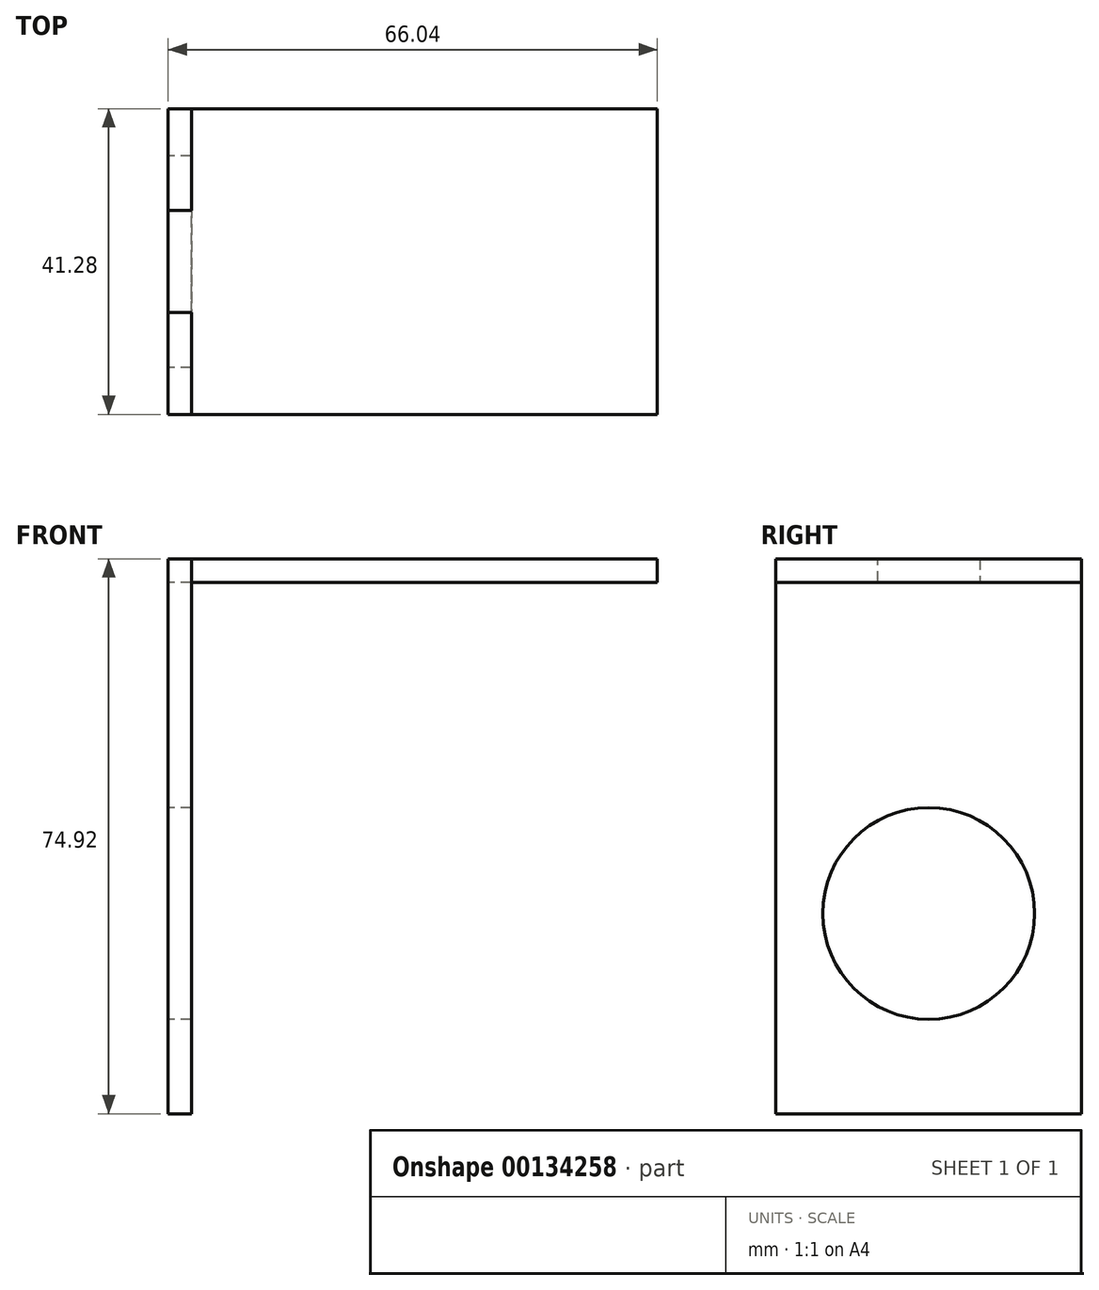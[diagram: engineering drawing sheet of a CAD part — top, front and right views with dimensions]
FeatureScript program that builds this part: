
annotation { "Feature Type Name" : "Feature", "Feature Type Description" : "" }
export const myFeature = defineFeature(function(context is Context, id is Id, definition is map)
    precondition{}
    {
        {
            var Q0;
            Q0=qCreatedBy(makeId("Top.planeOp"),FACE);
            var sketch = newSketch(context, id + "F0", { "sketchPlane" : qUnion([Q0])});
            skLineSegment(sketch, "E0.bottom", {"start": v(-33.02, 20.64) * mm, "end": v(33.02, 20.64) * mm});
            skLineSegment(sketch, "E0.top", {"start": v(-33.02, -20.64) * mm, "end": v(33.02, -20.64) * mm});
            skLineSegment(sketch, "E0.left", {"start": v(-33.02, 20.64) * mm, "end": v(-33.02, -20.64) * mm});
            skLineSegment(sketch, "E0.right", {"start": v(33.02, 20.64) * mm, "end": v(33.02, -20.64) * mm});
            skPoint(sketch, "E0.middle", {"position": v(0, 0) * mm});
            skSolve(sketch);
        }
        {
            var Q0;
            Q0=qSketchRegion(id+"F0",true);
            extrude(context, id + "F1", {"entities" : qUnion([Q0]), "depth" : 3.17 * mm});
        }
        {
            var Q0;
            Q0=makeQuery(id+"F1.opExtrude","CAP_FACE",FACE,{"disambiguationData":[OSD([sQuery(id+"F0.wireOp",EDGE,"E0.bottom"),sQuery(id+"F0.wireOp",EDGE,"E0.top"),sQuery(id+"F0.wireOp",EDGE,"E0.left"),sQuery(id+"F0.wireOp",EDGE,"E0.right")])],"isStart":true});
            var sketch = newSketch(context, id + "F2", { "sketchPlane" : qUnion([Q0])});
            skLineSegment(sketch, "E1.bottom", {"start": v(-33.02, 20.64) * mm, "end": v(-29.85, 20.64) * mm});
            skLineSegment(sketch, "E1.top", {"start": v(-33.02, -20.64) * mm, "end": v(-29.85, -20.64) * mm});
            skLineSegment(sketch, "E1.left", {"start": v(-33.02, 20.64) * mm, "end": v(-33.02, -20.64) * mm});
            skLineSegment(sketch, "E1.right", {"start": v(-29.85, 20.64) * mm, "end": v(-29.85, -20.64) * mm});
            skSolve(sketch);
        }
        {
            var Q0;
            Q0=qSketchRegion(id+"F2",true);
            extrude(context, id + "F3", {"entities" : qUnion([Q0]), "depth" : 71.75 * mm});
        }
        {
            var Q0;
            Q0=makeQuery(id+"F1.opExtrude","SWEPT_FACE",FACE,{"disambiguationData":[OSD([sQuery(id+"F0.wireOp",EDGE,"E0.left")])]});
            var sketch = newSketch(context, id + "F4", { "sketchPlane" : qUnion([Q0])});
            skLineSegment(sketch, "E2.bottom", {"start": v(-20.64, 3.18) * mm, "end": v(-6.88, 3.18) * mm});
            skLineSegment(sketch, "E2.top", {"start": v(-20.64, 0) * mm, "end": v(-6.88, 0) * mm});
            skLineSegment(sketch, "E2.left", {"start": v(-20.64, 3.18) * mm, "end": v(-20.64, 0) * mm});
            skLineSegment(sketch, "E2.right", {"start": v(-6.88, 3.18) * mm, "end": v(-6.88, 0) * mm});
            skLineSegment(sketch, "E3.bottom", {"start": v(-6.88, 0) * mm, "end": v(6.88, 0) * mm});
            skLineSegment(sketch, "E3.top", {"start": v(-6.88, 3.18) * mm, "end": v(6.88, 3.18) * mm});
            skLineSegment(sketch, "E3.left", {"start": v(-6.88, 0) * mm, "end": v(-6.88, 3.18) * mm});
            skLineSegment(sketch, "E3.right", {"start": v(6.88, 0) * mm, "end": v(6.88, 3.18) * mm});
            skLineSegment(sketch, "E4.bottom", {"start": v(6.88, 3.18) * mm, "end": v(20.64, 3.18) * mm});
            skLineSegment(sketch, "E4.top", {"start": v(6.88, 0) * mm, "end": v(20.64, 0) * mm});
            skLineSegment(sketch, "E4.left", {"start": v(6.88, 3.18) * mm, "end": v(6.88, 0) * mm});
            skLineSegment(sketch, "E4.right", {"start": v(20.64, 3.18) * mm, "end": v(20.64, 0) * mm});
            skSolve(sketch);
        }
        {
            var Q0;
            Q0=makeQuery(id+"F4.imprint","IMPRINT",FACE,{"disambiguationData":[TD([[makeQuery(id+"F4.imprint","IMPRINT",EDGE,{"derivedFrom":sQuery(id+"F4.wireOp",EDGE,"E2.bottom")}),-1.0]])]});
            var Q1;
            Q1=makeQuery(id+"F4.imprint","IMPRINT",FACE,{"disambiguationData":[TD([[makeQuery(id+"F4.imprint","IMPRINT",EDGE,{"derivedFrom":sQuery(id+"F4.wireOp",EDGE,"E4.bottom")}),-1.0]])]});
            extrude(context, id + "F5", {"entities" : qUnion([Q0, Q1]), "oppositeDirection" : true, "depth" : 3.17 * mm});
        }
        {
            var Q0;
            Q0=makeQuery(id+"F5.opExtrude","SWEPT_BODY",BODY,{"disambiguationData":[OSD([sQuery(id+"F4.wireOp",EDGE,"E4.bottom"),sQuery(id+"F4.wireOp",EDGE,"E4.top"),sQuery(id+"F4.wireOp",EDGE,"E4.left"),sQuery(id+"F4.wireOp",EDGE,"E4.right")])]});
            var Q1;
            Q1=makeQuery(id+"F5.opExtrude","SWEPT_BODY",BODY,{"disambiguationData":[OSD([sQuery(id+"F4.wireOp",EDGE,"E2.bottom"),sQuery(id+"F4.wireOp",EDGE,"E2.top"),sQuery(id+"F4.wireOp",EDGE,"E2.left"),sQuery(id+"F4.wireOp",EDGE,"E3.left")])]});
            var Q2;
            Q2=makeQuery(id+"F1.opExtrude","SWEPT_BODY",BODY,{"disambiguationData":[OSD([sQuery(id+"F0.wireOp",EDGE,"E0.bottom"),sQuery(id+"F0.wireOp",EDGE,"E0.top"),sQuery(id+"F0.wireOp",EDGE,"E0.left"),sQuery(id+"F0.wireOp",EDGE,"E0.right")])]});
            booleanBodies(context, id + "F6", {"operationType" : BooleanOperationType.SUBTRACTION, "tools" : qUnion([Q0, Q1]), "targets" : qUnion([Q2]), "keepTools" : true});
        }
        {
            var Q0;
            Q0=makeQuery(id+"F5.opExtrude","SWEPT_BODY",BODY,{"disambiguationData":[OSD([sQuery(id+"F4.wireOp",EDGE,"E4.bottom"),sQuery(id+"F4.wireOp",EDGE,"E4.top"),sQuery(id+"F4.wireOp",EDGE,"E4.left"),sQuery(id+"F4.wireOp",EDGE,"E4.right")])]});
            var Q1;
            Q1=makeQuery(id+"F3.opExtrude","SWEPT_BODY",BODY,{"disambiguationData":[OSD([sQuery(id+"F2.wireOp",EDGE,"E1.bottom"),sQuery(id+"F2.wireOp",EDGE,"E1.top"),sQuery(id+"F2.wireOp",EDGE,"E1.left"),sQuery(id+"F2.wireOp",EDGE,"E1.right")])]});
            var Q2;
            Q2=makeQuery(id+"F5.opExtrude","SWEPT_BODY",BODY,{"disambiguationData":[OSD([sQuery(id+"F4.wireOp",EDGE,"E2.bottom"),sQuery(id+"F4.wireOp",EDGE,"E2.top"),sQuery(id+"F4.wireOp",EDGE,"E2.left"),sQuery(id+"F4.wireOp",EDGE,"E3.left")])]});
            booleanBodies(context, id + "F7", {"operationType" : BooleanOperationType.UNION, "tools" : qUnion([Q0, Q1, Q2])});
        }
        {
            var Q0;
            Q0=makeQuery(id+"F7.opBoolean","MERGE",FACE,{"derivedFrom":[makeQuery(id+"F3.opExtrude","SWEPT_FACE",FACE,{"disambiguationData":[OSD([sQuery(id+"F2.wireOp",EDGE,"E1.left")])]}),makeQuery(id+"F5.opExtrude","CAP_FACE",FACE,{"disambiguationData":[OSD([sQuery(id+"F4.wireOp",EDGE,"E2.bottom"),sQuery(id+"F4.wireOp",EDGE,"E2.top"),sQuery(id+"F4.wireOp",EDGE,"E2.left"),sQuery(id+"F4.wireOp",EDGE,"E3.left")])],"isStart":true}),makeQuery(id+"F5.opExtrude","CAP_FACE",FACE,{"disambiguationData":[OSD([sQuery(id+"F4.wireOp",EDGE,"E4.bottom"),sQuery(id+"F4.wireOp",EDGE,"E4.top"),sQuery(id+"F4.wireOp",EDGE,"E4.left"),sQuery(id+"F4.wireOp",EDGE,"E4.right")])],"isStart":true})]});
            var sketch = newSketch(context, id + "F8", { "sketchPlane" : qUnion([Q0])});
            skCircle(sketch, "E5", {"center": v(0, -44.7) * mm, "radius": 14.29 * mm});
            skSolve(sketch);
        }
        {
            var Q0;
            Q0=makeQuery(id+"F8.imprint","IMPRINT",FACE,{"disambiguationData":[TD([[makeQuery(id+"F8.imprint","IMPRINT",EDGE,{"derivedFrom":sQuery(id+"F8.wireOp",EDGE,"E5")}),1.0]])]});
            extrude(context, id + "F9", {"entities" : qUnion([Q0]), "operationType" : NewBodyOperationType.REMOVE, "endBound" : BoundingType.THROUGH_ALL, "oppositeDirection" : true, "depth" : 25.4 * mm});
        }
    });
